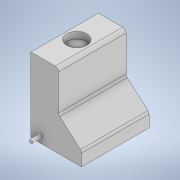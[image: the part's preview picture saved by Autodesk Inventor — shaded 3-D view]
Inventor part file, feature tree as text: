
AUTODESK INVENTOR PART (.ipt)
format: ipt  version: 2021 (Build 250183000, 183)  size: 128,000 bytes
history: native  units: mm
features: sketch x7, extrude x5, fillet x1
ambient origin geometry x8: Origin, YZ Plane, XZ Plane, XY Plane, X Axis, Y Axis, Z Axis, Center Point
bodies: Body1 (feature_tree)
feature tree (13):
  extrude  "Extrusion9"  Depth=150.0mm
  extrude  "Extrusion11"  Depth=200.0mm
  fillet  "Fillet3"  Radius=200.0mm
  extrude  "Extrusion12"  Depth=200.0mm TaperAngle=0.0deg
  sketch  "Sketch22"  dims[d84=10.0mm d85=60.0mm]
  sketch  "Sketch23"  dims[d86=20.0mm d87=0.0mm d88=30.0mm d89=0.0mm]
  extrude  "Extrusion13"  Depth=10.0mm
  extrude  "Extrusion14"  Depth=30.0mm TaperAngle=0.0deg
  sketch  "Sketch18"  dims[d72=220.0mm d73=150.0mm]
  sketch  "Sketch20"  dims[d74=120.0mm d75=40.0mm d76=200.0mm d77=0.0mm]
  sketch  "Sketch21"  dims[d81=10.0mm d82=200.0mm d83=0.0mm]
  sketch  "Sketch24"  dims[d90=30.0mm d91=0.0mm]
  sketch  "Sketch25"
